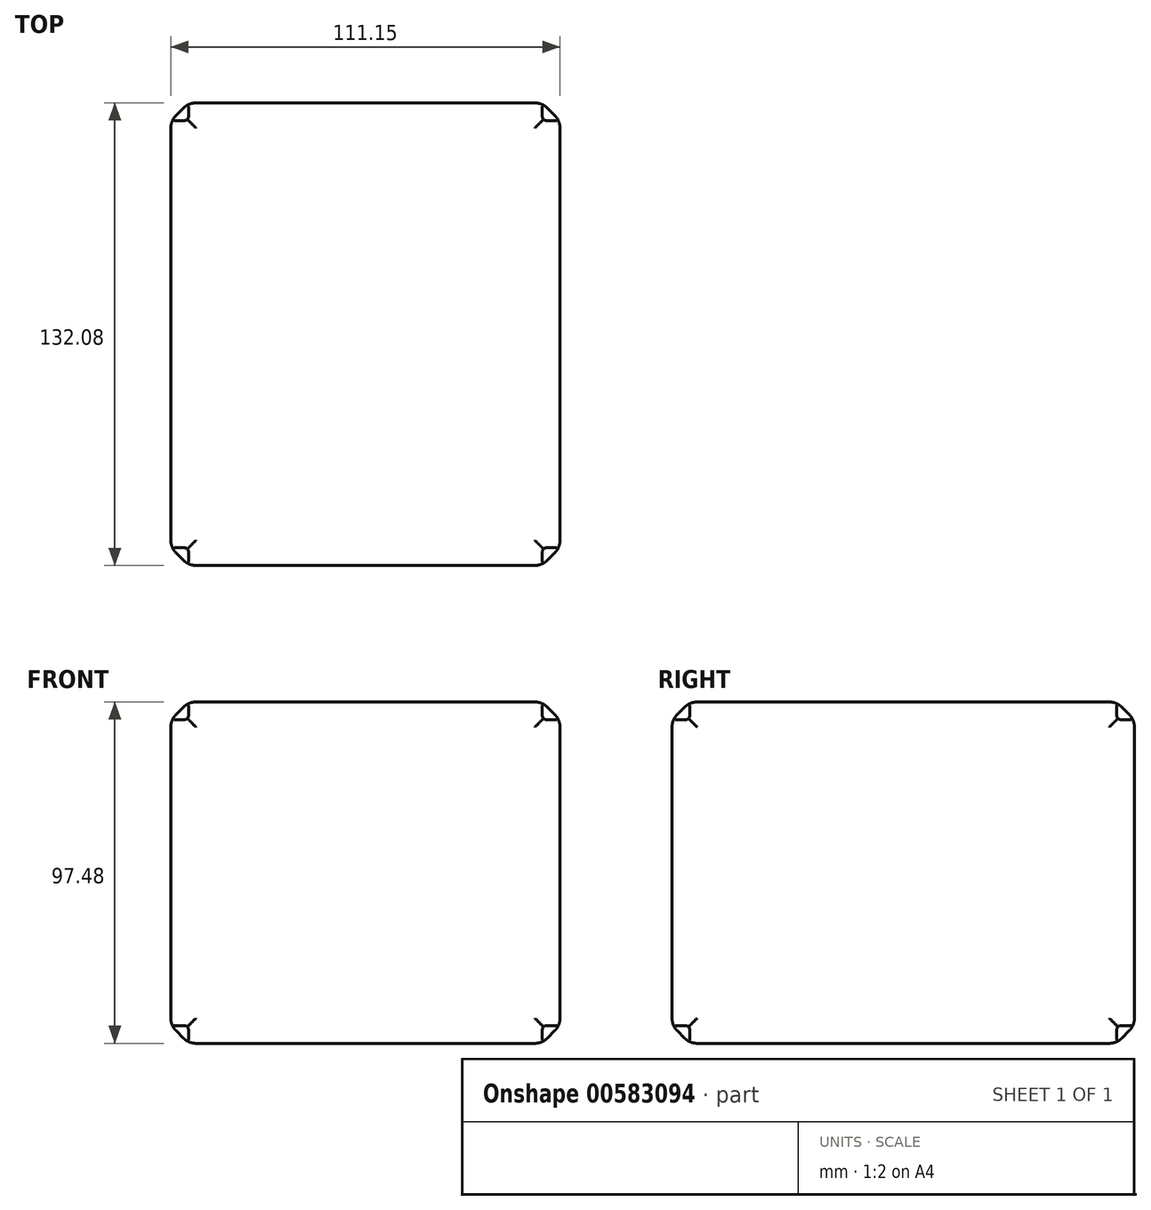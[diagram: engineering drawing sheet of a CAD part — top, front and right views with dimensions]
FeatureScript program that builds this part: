
annotation { "Feature Type Name" : "Feature", "Feature Type Description" : "" }
export const myFeature = defineFeature(function(context is Context, id is Id, definition is map)
    precondition{}
    {
        {
            var Q0;
            Q0=qCreatedBy(makeId("Front.planeOp"),FACE);
            var sketch = newSketch(context, id + "F0", { "sketchPlane" : qUnion([Q0])});
            skLineSegment(sketch, "E0.bottom", {"start": v(-55.75, 50.08) * mm, "end": v(55.4, 50.08) * mm});
            skLineSegment(sketch, "E0.top", {"start": v(-55.75, -47.4) * mm, "end": v(55.4, -47.4) * mm});
            skLineSegment(sketch, "E0.left", {"start": v(-55.75, 50.08) * mm, "end": v(-55.75, -47.4) * mm});
            skLineSegment(sketch, "E0.right", {"start": v(55.4, 50.08) * mm, "end": v(55.4, -47.4) * mm});
            skSolve(sketch);
        }
        {
            var Q0;
            Q0=makeQuery(id+"F0.imprint","IMPRINT",FACE,{"disambiguationData":[TD([[makeQuery(id+"F0.imprint","IMPRINT",EDGE,{"derivedFrom":sQuery(id+"F0.wireOp",EDGE,"E0.bottom")}),-1.0]])]});
            extrude(context, id + "F1", {"entities" : qUnion([Q0]), "depth" : 132.08 * mm, "offsetDistance" : 25.4 * mm});
        }
        {
            var Q0;
            Q0=makeQuery(id+"F1.opExtrude","SWEPT_FACE",FACE,{"disambiguationData":[OSD([sQuery(id+"F0.wireOp",EDGE,"E0.bottom")])]});
            var Q1;
            Q1=makeQuery(id+"F1.opExtrude","SWEPT_FACE",FACE,{"disambiguationData":[OSD([sQuery(id+"F0.wireOp",EDGE,"E0.right")])]});
            var Q2;
            Q2=makeQuery(id+"F1.opExtrude","CAP_FACE",FACE,{"disambiguationData":[OSD([sQuery(id+"F0.wireOp",EDGE,"E0.bottom"),sQuery(id+"F0.wireOp",EDGE,"E0.top"),sQuery(id+"F0.wireOp",EDGE,"E0.left"),sQuery(id+"F0.wireOp",EDGE,"E0.right")])],"isStart":false});
            var Q3;
            Q3=makeQuery(id+"F1.opExtrude","SWEPT_FACE",FACE,{"disambiguationData":[OSD([sQuery(id+"F0.wireOp",EDGE,"E0.top")])]});
            var Q4;
            Q4=makeQuery(id+"F1.opExtrude","SWEPT_FACE",FACE,{"disambiguationData":[OSD([sQuery(id+"F0.wireOp",EDGE,"E0.left")])]});
            chamfer(context, id + "F2", {"entities" : qUnion([Q0, Q1, Q2, Q3, Q4]), "width" : 5.08 * mm, "tangentPropagation" : true});
        }
        {
            var Q0;
            Q0=makeQuery(id+"F1.opExtrude","SWEPT_FACE",FACE,{"disambiguationData":[OSD([sQuery(id+"F0.wireOp",EDGE,"E0.bottom")])]});
            var Q1;
            Q1=makeQuery(id+"F1.opExtrude","CAP_FACE",FACE,{"disambiguationData":[OSD([sQuery(id+"F0.wireOp",EDGE,"E0.bottom"),sQuery(id+"F0.wireOp",EDGE,"E0.top"),sQuery(id+"F0.wireOp",EDGE,"E0.left"),sQuery(id+"F0.wireOp",EDGE,"E0.right")])],"isStart":true});
            var Q2;
            Q2=makeQuery(id+"F1.opExtrude","SWEPT_FACE",FACE,{"disambiguationData":[OSD([sQuery(id+"F0.wireOp",EDGE,"E0.right")])]});
            var Q3;
            Q3=makeQuery(id+"F1.opExtrude","SWEPT_FACE",FACE,{"disambiguationData":[OSD([sQuery(id+"F0.wireOp",EDGE,"E0.top")])]});
            var Q4;
            Q4=makeQuery(id+"F1.opExtrude","SWEPT_FACE",FACE,{"disambiguationData":[OSD([sQuery(id+"F0.wireOp",EDGE,"E0.left")])]});
            var Q5;
            Q5=makeQuery(id+"F1.opExtrude","CAP_FACE",FACE,{"disambiguationData":[OSD([sQuery(id+"F0.wireOp",EDGE,"E0.bottom"),sQuery(id+"F0.wireOp",EDGE,"E0.top"),sQuery(id+"F0.wireOp",EDGE,"E0.left"),sQuery(id+"F0.wireOp",EDGE,"E0.right")])],"isStart":false});
            fillet(context, id + "F3", {"entities" : qUnion([Q0, Q1, Q2, Q3, Q4, Q5]), "radius" : 5.08 * mm, "tangentPropagation" : true, "allowEdgeOverflow" : false});
        }
    });
